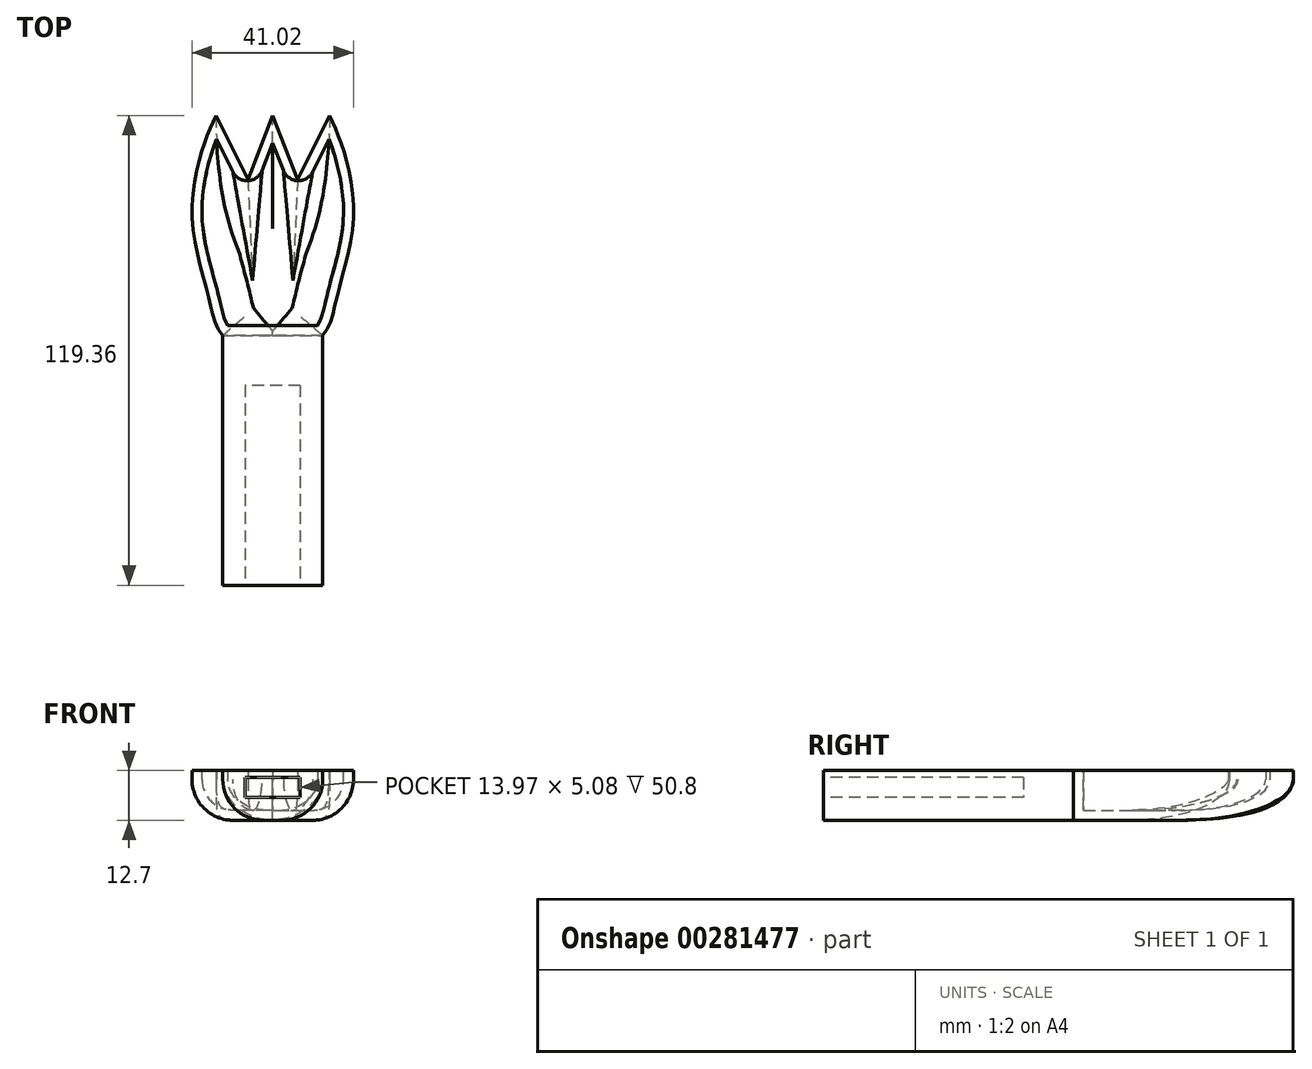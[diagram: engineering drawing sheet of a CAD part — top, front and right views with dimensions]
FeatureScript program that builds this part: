
annotation { "Feature Type Name" : "Feature", "Feature Type Description" : "" }
export const myFeature = defineFeature(function(context is Context, id is Id, definition is map)
    precondition{}
    {
        {
            var Q0;
            Q0=qCreatedBy(makeId("Top.planeOp"),FACE);
            var sketch = newSketch(context, id + "F0", { "sketchPlane" : qUnion([Q0])});
            skLineSegment(sketch, "E0", {"start": v(0, 75.51) * mm, "end": v(0, -68.28) * mm});
            skFitSpline(sketch, "E1", {"points": [v(0, -14.97) * mm, v(-12.7, -14.95) * mm], "startDerivative": vector(-9.63, -0.3) * mm, "endDerivative": vector(-10.55, 0.04) * mm});
            skFitSpline(sketch, "E2", {"points": [v(-12.7, -14.95) * mm, v(-16.24, -5.41) * mm, v(-20.45, 14.44) * mm, v(-17.75, 32.79) * mm, v(-14.44, 40.9) * mm], "startDerivative": vector(-31.58, 37.42) * mm, "endDerivative": vector(17.48, 37.1) * mm});
            skLineSegment(sketch, "E3", {"start": v(-14.44, 40.9) * mm, "end": v(-6.32, 24.67) * mm});
            skLineSegment(sketch, "E4", {"start": v(-6.32, 24.67) * mm, "end": v(0, 40.9) * mm});
            skLineSegment(sketch, "E5", {"start": v(-12.7, -14.95) * mm, "end": v(-12.7, -78.45) * mm});
            skLineSegment(sketch, "E6", {"start": v(-12.7, -78.45) * mm, "end": v(0, -78.45) * mm});
            skLineSegment(sketch, "E7", {"start": v(0, -78.45) * mm, "end": v(0, -14.97) * mm});
            skSolve(sketch);
        }
        {
            var Q0;
            {var subQ0=sQuery(id+"F0.wireOp",EDGE,"E1");Q0=makeQuery(id+"F0.imprint","IMPRINT",FACE,{"disambiguationData":[TD([[makeQuery(id+"F0.imprint","IMPRINT",EDGE,{"derivedFrom":subQ0}),-1.0]])]});}
            extrude(context, id + "F1", {"entities" : qUnion([Q0]), "depth" : 12.7 * mm});
        }
        {
            var Q0;
            Q0=makeQuery(id+"F1.opExtrude","CAP_EDGE",EDGE,{"disambiguationData":[OSD([sQuery(id+"F0.wireOp",EDGE,"E2")])],"isStart":true});
            var Q1;
            Q1=makeQuery(id+"F1.opExtrude","CAP_EDGE",EDGE,{"disambiguationData":[OSD([sQuery(id+"F0.wireOp",EDGE,"E3")])],"isStart":true});
            var Q2;
            Q2=makeQuery(id+"F1.opExtrude","CAP_EDGE",EDGE,{"disambiguationData":[OSD([sQuery(id+"F0.wireOp",EDGE,"E4")])],"isStart":true});
            fillet(context, id + "F2", {"entities" : qUnion([Q0, Q1, Q2]), "radius" : 10.4 * mm, "tangentPropagation" : true, "allowEdgeOverflow" : false});
        }
        {
            var Q0;
            Q0=makeQuery(id+"F1.opExtrude","SWEPT_BODY",BODY,{"disambiguationData":[OSD([sQuery(id+"F0.wireOp",EDGE,"E0"),sQuery(id+"F0.wireOp",EDGE,"E1"),sQuery(id+"F0.wireOp",EDGE,"E2"),sQuery(id+"F0.wireOp",EDGE,"E3"),sQuery(id+"F0.wireOp",EDGE,"E4")])]});
            var Q1;
            Q1=makeQuery(id+"F1.opExtrude","SWEPT_FACE",FACE,{"disambiguationData":[OSD([sQuery(id+"F0.wireOp",EDGE,"E0")])]});
            mirror(context, id + "F3", {"operationType" : NewBodyOperationType.ADD, "entities" : qUnion([Q0]), "mirrorPlane" : qUnion([Q1])});
        }
        {
            var Q0;
            {var subQ0=makeQuery(id+"F1.opExtrude","CAP_FACE",FACE,{"disambiguationData":[OSD([sQuery(id+"F0.wireOp",EDGE,"E0"),sQuery(id+"F0.wireOp",EDGE,"E1"),sQuery(id+"F0.wireOp",EDGE,"E2"),sQuery(id+"F0.wireOp",EDGE,"E3"),sQuery(id+"F0.wireOp",EDGE,"E4")])],"isStart":false});Q0=makeQuery(id+"F3.boolean.opBoolean","MERGE",FACE,{"derivedFrom":[subQ0,makeQuery(id+"F3.opPattern","COPY",FACE,{"derivedFrom":subQ0,"instanceName":"1"})]});}
            var Q1;
            Q1=makeQuery(id+"F1.opExtrude","SWEPT_BODY",BODY,{"disambiguationData":[OSD([sQuery(id+"F0.wireOp",EDGE,"E0"),sQuery(id+"F0.wireOp",EDGE,"E1"),sQuery(id+"F0.wireOp",EDGE,"E2"),sQuery(id+"F0.wireOp",EDGE,"E3"),sQuery(id+"F0.wireOp",EDGE,"E4")])]});
            shell(context, id + "F4", {"entities" : qUnion([Q0]), "parts" : qUnion([Q1]), "thickness" : 2.54 * mm});
        }
        {
            var Q0;
            {var subQ0=sQuery(id+"F0.wireOp",EDGE,"E4");var subQ1=sQuery(id+"F0.wireOp",EDGE,"E3");Q0=makeQuery(id+"F4.opShell","OFFSET_EDGE",EDGE,{"disambiguationData":[OSD([subQ1,subQ0]),TDD([makeQuery(id+"F3.opPattern","COPY",EDGE,{"derivedFrom":makeQuery(id+"F2.opFillet","BLEND_EDGE",EDGE,{"blendedFrom":[makeQuery(id+"F1.opExtrude","CAP_EDGE",EDGE,{"disambiguationData":[OSD([subQ1])],"isStart":true}),makeQuery(id+"F1.opExtrude","CAP_EDGE",EDGE,{"disambiguationData":[OSD([subQ0])],"isStart":true})],"blendedInto":[]}),"instanceName":"1"})])]});}
            var Q1;
            {var subQ0=sQuery(id+"F0.wireOp",EDGE,"E4");var subQ1=sQuery(id+"F0.wireOp",EDGE,"E3");Q1=makeQuery(id+"F4.opShell","OFFSET_EDGE",EDGE,{"disambiguationData":[OSD([subQ1,subQ0]),TDD([makeQuery(id+"F2.opFillet","BLEND_EDGE",EDGE,{"blendedFrom":[makeQuery(id+"F1.opExtrude","CAP_EDGE",EDGE,{"disambiguationData":[OSD([subQ1])],"isStart":true}),makeQuery(id+"F1.opExtrude","CAP_EDGE",EDGE,{"disambiguationData":[OSD([subQ0])],"isStart":true})],"blendedInto":[]})])]});}
            fillet(context, id + "F5", {"entities" : qUnion([Q0, Q1]), "radius" : 4.06 * mm, "tangentPropagation" : true, "allowEdgeOverflow" : false});
        }
        {
            var Q0;
            {var subQ0=sQuery(id+"F0.wireOp",EDGE,"E1");Q0=makeQuery(id+"F0.imprint","IMPRINT",FACE,{"disambiguationData":[TD([[makeQuery(id+"F0.imprint","IMPRINT",EDGE,{"derivedFrom":subQ0}),1.0]])]});}
            extrude(context, id + "F6", {"entities" : qUnion([Q0]), "depth" : 12.7 * mm});
        }
        {
            var Q0;
            Q0=makeQuery(id+"F6.opExtrude","CAP_EDGE",EDGE,{"disambiguationData":[OSD([sQuery(id+"F0.wireOp",EDGE,"E5")])],"isStart":true});
            fillet(context, id + "F7", {"entities" : qUnion([Q0]), "radius" : 10.4 * mm, "tangentPropagation" : true, "allowEdgeOverflow" : false});
        }
        {
            var Q0;
            Q0=makeQuery(id+"F6.opExtrude","SWEPT_FACE",FACE,{"disambiguationData":[OSD([sQuery(id+"F0.wireOp",EDGE,"E6")])]});
            var sketch = newSketch(context, id + "F8", { "sketchPlane" : qUnion([Q0])});
            skLineSegment(sketch, "E8", {"start": v(0, 10.88) * mm, "end": v(-6.99, 10.88) * mm});
            skLineSegment(sketch, "E9", {"start": v(-6.99, 10.88) * mm, "end": v(-6.99, 5.8) * mm});
            skLineSegment(sketch, "E10", {"start": v(-6.99, 5.8) * mm, "end": v(0, 5.8) * mm});
            skLineSegment(sketch, "E11", {"start": v(0, 10.88) * mm, "end": v(0, 5.8) * mm});
            skSolve(sketch);
        }
        {
            var Q0;
            Q0=makeQuery(id+"F8.imprint","IMPRINT",FACE,{"disambiguationData":[TD([[makeQuery(id+"F8.imprint","IMPRINT",EDGE,{"derivedFrom":sQuery(id+"F8.wireOp",EDGE,"E8")}),1.0]])]});
            extrude(context, id + "F9", {"entities" : qUnion([Q0]), "operationType" : NewBodyOperationType.REMOVE, "oppositeDirection" : true, "depth" : 50.8 * mm});
        }
        {
            var Q0;
            Q0=makeQuery(id+"F6.opExtrude","SWEPT_BODY",BODY,{"disambiguationData":[OSD([sQuery(id+"F0.wireOp",EDGE,"E1"),sQuery(id+"F0.wireOp",EDGE,"E5"),sQuery(id+"F0.wireOp",EDGE,"E6"),sQuery(id+"F0.wireOp",EDGE,"E7")])]});
            var Q1;
            Q1=qCreatedBy(makeId("Right.planeOp"),FACE);
            mirror(context, id + "F10", {"operationType" : NewBodyOperationType.ADD, "entities" : qUnion([Q0]), "mirrorPlane" : qUnion([Q1])});
        }
    });
